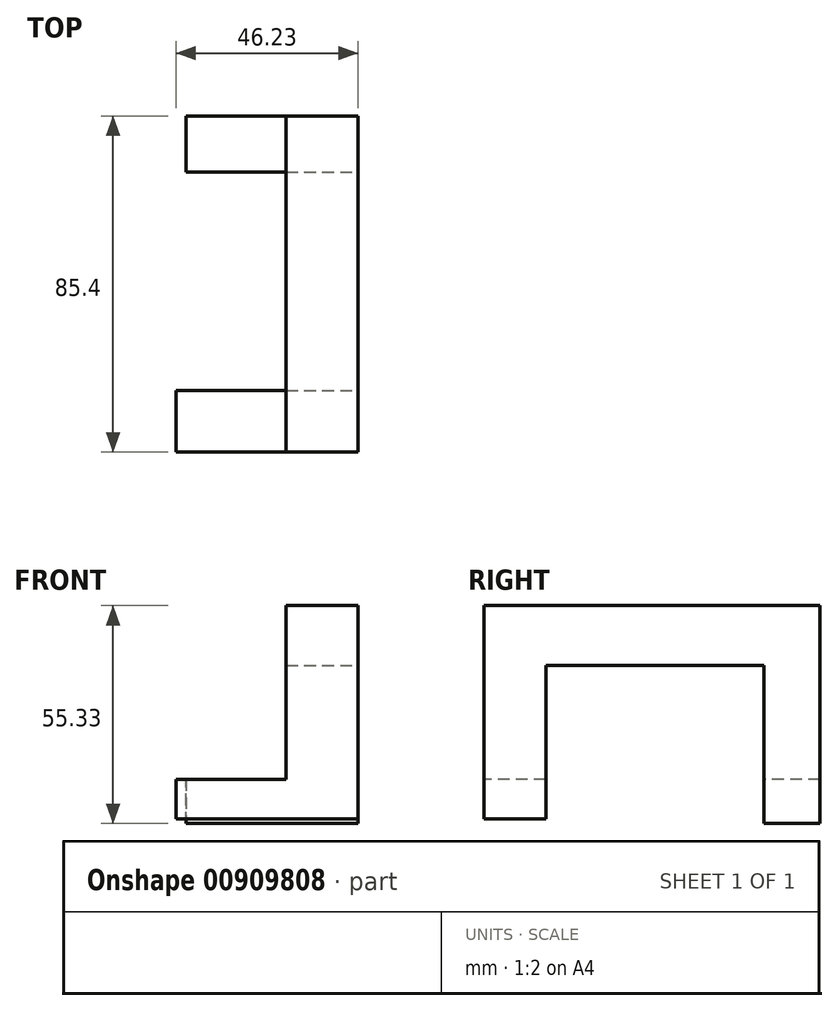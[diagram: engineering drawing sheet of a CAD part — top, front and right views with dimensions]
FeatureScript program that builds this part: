
annotation { "Feature Type Name" : "Feature", "Feature Type Description" : "" }
export const myFeature = defineFeature(function(context is Context, id is Id, definition is map)
    precondition{}
    {
        {
            var Q0;
            Q0=qCreatedBy(makeId("Right.planeOp"),FACE);
            var sketch = newSketch(context, id + "F0", { "sketchPlane" : qUnion([Q0])});
            skLineSegment(sketch, "E0", {"start": v(-44.88, -10.1) * mm, "end": v(-32.49, -10.1) * mm});
            skLineSegment(sketch, "E1", {"start": v(-32.49, -10.1) * mm, "end": v(-32.49, 28.93) * mm});
            skLineSegment(sketch, "E2", {"start": v(-32.49, 28.93) * mm, "end": v(26.29, 28.93) * mm});
            skLineSegment(sketch, "E3", {"start": v(26.29, 28.93) * mm, "end": v(26.29, -11.25) * mm});
            skLineSegment(sketch, "E4", {"start": v(26.29, -11.25) * mm, "end": v(40.52, -11.25) * mm});
            skLineSegment(sketch, "E5", {"start": v(40.52, -11.25) * mm, "end": v(40.52, 44.08) * mm});
            skLineSegment(sketch, "E6", {"start": v(40.52, 44.08) * mm, "end": v(-44.88, 44.08) * mm});
            skLineSegment(sketch, "E7", {"start": v(-44.88, 44.08) * mm, "end": v(-44.88, -10.1) * mm});
            skSolve(sketch);
        }
        {
            var Q0;
            Q0 = qSketchRegion(id + "F0", true);
            extrude(context, id + "F1", {"entities" : qUnion([Q0]), "oppositeDirection" : true, "depth" : 18.29 * mm, "offsetDistance" : 25.4 * mm});
        }
        {
            var Q0;
            Q0=makeQuery(id+"F1.opExtrude","CAP_FACE",FACE,{"disambiguationData":[OSD([sQuery(id+"F0.wireOp",EDGE,"E0"),sQuery(id+"F0.wireOp",EDGE,"E1"),sQuery(id+"F0.wireOp",EDGE,"E2"),sQuery(id+"F0.wireOp",EDGE,"E3"),sQuery(id+"F0.wireOp",EDGE,"E4"),sQuery(id+"F0.wireOp",EDGE,"E5"),sQuery(id+"F0.wireOp",EDGE,"E6"),sQuery(id+"F0.wireOp",EDGE,"E7")])],"isStart":false});
            var sketch = newSketch(context, id + "F2", { "sketchPlane" : qUnion([Q0])});
            skLineSegment(sketch, "E8", {"start": v(-40.52, 0) * mm, "end": v(-26.29, 0) * mm});
            skLineSegment(sketch, "E9", {"start": v(-26.29, 0) * mm, "end": v(-26.29, -11.25) * mm});
            skLineSegment(sketch, "E10", {"start": v(-26.29, -11.25) * mm, "end": v(-40.52, -11.25) * mm});
            skLineSegment(sketch, "E11", {"start": v(-40.52, -11.25) * mm, "end": v(-40.52, 0) * mm});
            skSolve(sketch);
        }
        {
            var Q0;
            Q0 = qSketchRegion(id + "F2", true);
            extrude(context, id + "F3", {"entities" : qUnion([Q0]), "operationType" : NewBodyOperationType.ADD, "depth" : 25.4 * mm, "offsetDistance" : 25.4 * mm});
        }
        {
            var Q0;
            Q0=makeQuery(id+"F1.opExtrude","CAP_FACE",FACE,{"disambiguationData":[OSD([sQuery(id+"F0.wireOp",EDGE,"E0"),sQuery(id+"F0.wireOp",EDGE,"E1"),sQuery(id+"F0.wireOp",EDGE,"E2"),sQuery(id+"F0.wireOp",EDGE,"E3"),sQuery(id+"F0.wireOp",EDGE,"E4"),sQuery(id+"F0.wireOp",EDGE,"E5"),sQuery(id+"F0.wireOp",EDGE,"E6"),sQuery(id+"F0.wireOp",EDGE,"E7")])],"isStart":false});
            var sketch = newSketch(context, id + "F4", { "sketchPlane" : qUnion([Q0])});
            skLineSegment(sketch, "E12", {"start": v(32.49, 0) * mm, "end": v(44.88, 0) * mm});
            skLineSegment(sketch, "E13", {"start": v(44.88, 0) * mm, "end": v(44.88, -10.1) * mm});
            skLineSegment(sketch, "E14", {"start": v(44.88, -10.1) * mm, "end": v(32.49, -10.1) * mm});
            skLineSegment(sketch, "E15", {"start": v(32.49, -10.1) * mm, "end": v(32.49, 0) * mm});
            skSolve(sketch);
        }
        {
            var Q0;
            Q0 = qSketchRegion(id + "F4", true);
            extrude(context, id + "F5", {"entities" : qUnion([Q0]), "operationType" : NewBodyOperationType.ADD, "depth" : 27.94 * mm, "offsetDistance" : 25.4 * mm});
        }
        {
            var Q0;
            Q0=makeQuery(id+"F5.boolean.opBoolean","MERGE",FACE,{"derivedFrom":[makeQuery(id+"F1.opExtrude","SWEPT_FACE",FACE,{"disambiguationData":[OSD([sQuery(id+"F0.wireOp",EDGE,"E1")])]}),makeQuery(id+"F5.opExtrude","SWEPT_FACE",FACE,{"disambiguationData":[OSD([sQuery(id+"F4.wireOp",EDGE,"E15")])]})]});
            extrude(context, id + "F6", {"entities" : qUnion([Q0]), "operationType" : NewBodyOperationType.ADD, "depth" : 3.3 * mm, "offsetDistance" : 25.4 * mm});
        }
    });
